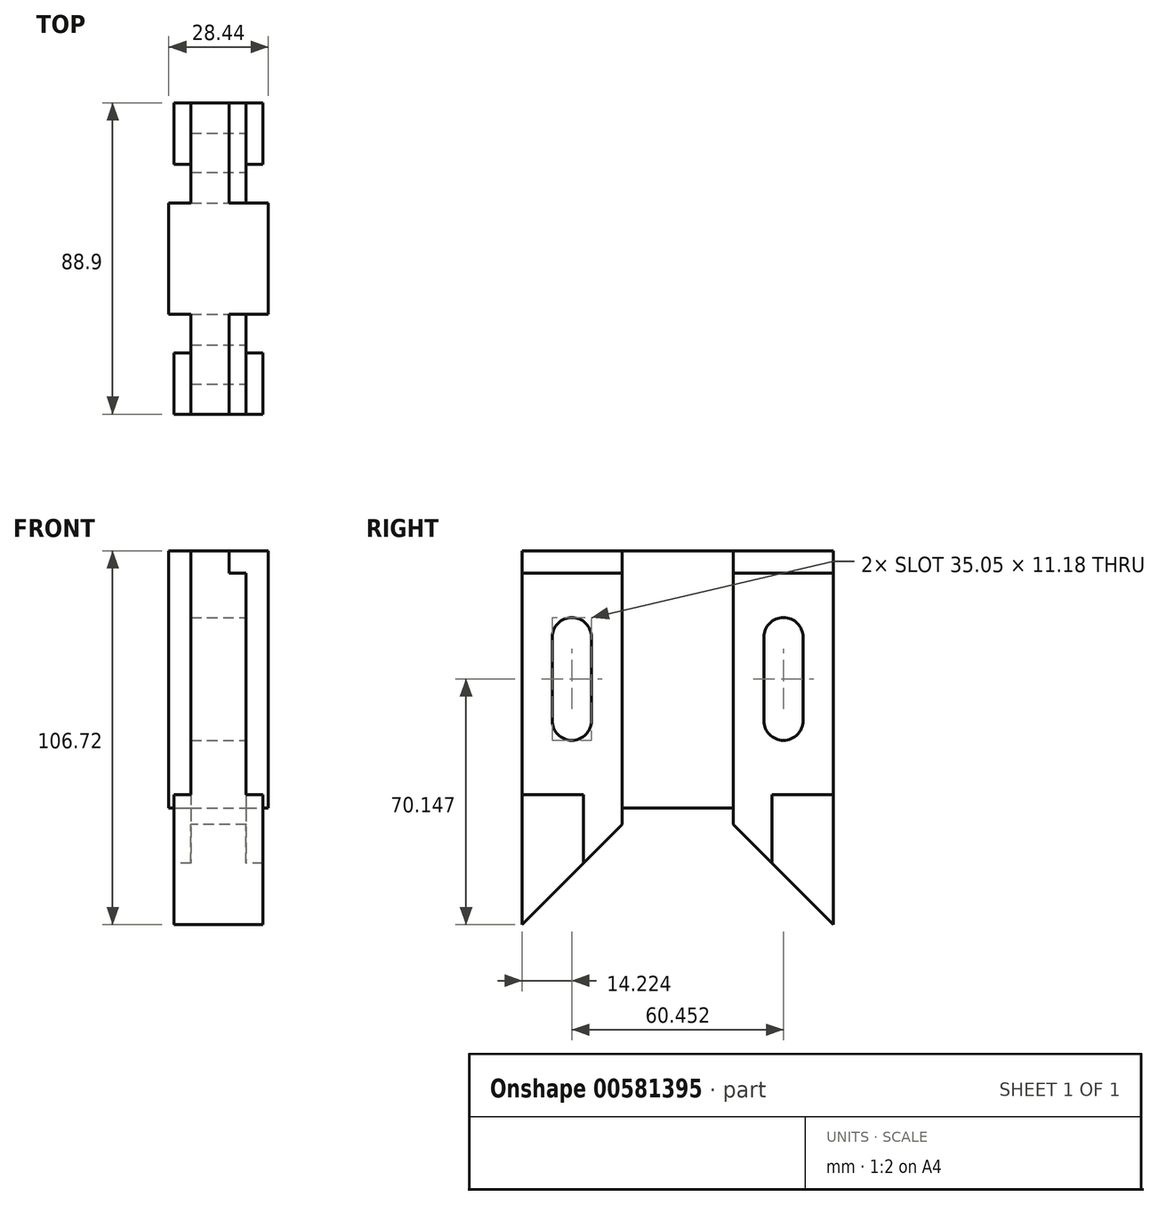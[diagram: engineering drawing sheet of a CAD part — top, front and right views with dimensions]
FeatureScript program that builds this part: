
annotation { "Feature Type Name" : "Feature", "Feature Type Description" : "" }
export const myFeature = defineFeature(function(context is Context, id is Id, definition is map)
    precondition{}
    {
        {
            var Q0;
            Q0=qCreatedBy(makeId("Front.planeOp"),FACE);
            var sketch = newSketch(context, id + "F0", { "sketchPlane" : qUnion([Q0])});
            skLineSegment(sketch, "E0.bottom", {"start": v(-14.22, -36.7) * mm, "end": v(14.22, -36.7) * mm});
            skLineSegment(sketch, "E0.top", {"start": v(-14.22, 36.7) * mm, "end": v(14.22, 36.7) * mm});
            skLineSegment(sketch, "E0.left", {"start": v(-14.22, -36.7) * mm, "end": v(-14.22, 36.7) * mm});
            skLineSegment(sketch, "E0.right", {"start": v(14.22, -36.7) * mm, "end": v(14.22, 36.7) * mm});
            skPoint(sketch, "E0.middle", {"position": v(0, 0) * mm});
            skLineSegment(sketch, "E1", {"start": v(0, 38.88) * mm, "end": v(0, -46.1) * mm, "construction": true});
            skPoint(sketch, "E1.endSnap0", {"position": v(0, -36.7) * mm});
            skSolve(sketch);
        }
        {
            var Q0;
            Q0 = qSketchRegion(id + "F0", true);
            extrude(context, id + "F1", {"entities" : qUnion([Q0]), "endBound" : BoundingType.SYMMETRIC, "depth" : 31.75 * mm, "offsetDistance" : 25.4 * mm});
        }
        {
            var Q0;
            Q0=qCreatedBy(makeId("Right.planeOp"),FACE);
            var sketch = newSketch(context, id + "F2", { "sketchPlane" : qUnion([Q0])});
            skLineSegment(sketch, "E2", {"start": v(-15.88, 36.7) * mm, "end": v(-44.45, 36.7) * mm});
            skLineSegment(sketch, "E3", {"start": v(-44.45, 36.7) * mm, "end": v(-44.45, 30.35) * mm});
            skLineSegment(sketch, "E4", {"start": v(-44.45, 30.35) * mm, "end": v(-15.88, 30.35) * mm});
            skLineSegment(sketch, "E5", {"start": v(-15.88, 30.35) * mm, "end": v(-15.88, 36.7) * mm});
            skLineSegment(sketch, "E6", {"start": v(-44.45, 30.35) * mm, "end": v(-44.45, -32.9) * mm});
            skLineSegment(sketch, "E7", {"start": v(-44.45, -32.9) * mm, "end": v(-26.92, -32.9) * mm});
            skLineSegment(sketch, "E8", {"start": v(-26.92, -32.9) * mm, "end": v(-26.92, -52.49) * mm});
            skLineSegment(sketch, "E9", {"start": v(-15.88, 36.7) * mm, "end": v(-15.88, -41.44) * mm});
            skLineSegment(sketch, "E10", {"start": v(-26.92, -52.49) * mm, "end": v(-15.87, -41.44) * mm});
            skPoint(sketch, "E11.0.1.end.orphan", {"position": v(-15.88, -36.7) * mm});
            skPoint(sketch, "E11.0.0.end.orphan", {"position": v(15.88, -36.7) * mm});
            skPoint(sketch, "E11.0.3.end.orphan", {"position": v(15.88, 36.7) * mm});
            skLineSegment(sketch, "E12.0.2", {"start": v(-15.88, -36.7) * mm, "end": v(-15.88, 36.7) * mm});
            skLineSegment(sketch, "E13", {"start": v(-78.92, 0) * mm, "end": v(0, 0) * mm, "construction": true});
            skLineSegment(sketch, "E14", {"start": v(0, 49.12) * mm, "end": v(0, -58.82) * mm, "construction": true});
            skLineSegment(sketch, "E15.left", {"start": v(-15.88, 36.7) * mm, "end": v(-15.87, -41.44) * mm});
            skLineSegment(sketch, "E15.right", {"start": v(-44.45, 36.7) * mm, "end": v(-44.45, -32.9) * mm});
            skPoint(sketch, "E16.end.orphan", {"position": v(-17.95, -70.02) * mm});
            skPoint(sketch, "E17.orphan", {"position": v(-44.45, -70.02) * mm});
            skSolve(sketch);
        }
        {
            var Q0;
            {var subQ5=sQuery(id+"F2.wireOp",EDGE,"E4");Q0=makeQuery(id+"F2.imprint","IMPRINT",FACE,{"disambiguationData":[TD([[makeQuery(id+"F2.imprint","IMPRINT",EDGE,{"derivedFrom":subQ5}),-1.0]])]});}
            var Q1;
            {var subQ0=sQuery(id+"F2.wireOp",EDGE,"E4");Q1=makeQuery(id+"F2.imprint","IMPRINT",FACE,{"disambiguationData":[TD([[makeQuery(id+"F2.imprint","IMPRINT",EDGE,{"derivedFrom":subQ0}),1.0]])]});}
            extrude(context, id + "F3", {"entities" : qUnion([Q0, Q1]), "operationType" : NewBodyOperationType.ADD, "endBound" : BoundingType.SYMMETRIC, "depth" : 15.75 * mm, "offsetDistance" : 25.4 * mm});
        }
        {
            var Q0;
            Q0=makeQuery(id+"F3.opExtrude","CAP_FACE",FACE,{"disambiguationData":[OSD([sQuery(id+"F2.wireOp",EDGE,"E7"),sQuery(id+"F2.wireOp",EDGE,"E8"),sQuery(id+"F2.wireOp",EDGE,"E10"),sQuery(id+"F2.wireOp",EDGE,"E2"),sQuery(id+"F2.wireOp",EDGE,"E15.left"),sQuery(id+"F2.wireOp",EDGE,"E15.right")])],"isStart":false});
            cPlane(context, id + "F4", {"entities" : qUnion([Q0]), "cplaneType" : CPlaneType.OFFSET, "offset" : 0 * mm, "width" : 152.4 * mm, "height" : 152.4 * mm});
        }
        {
            var Q0;
            Q0=qCreatedBy(id+"F4.planeOp",FACE);
            var sketch = newSketch(context, id + "F5", { "sketchPlane" : qUnion([Q0])});
            skLineSegment(sketch, "E18.0.0", {"start": v(-15.88, 30.35) * mm, "end": v(-15.88, 36.7) * mm});
            skLineSegment(sketch, "E18.0.1", {"start": v(-15.88, 36.7) * mm, "end": v(-44.45, 36.7) * mm});
            skLineSegment(sketch, "E18.0.2", {"start": v(-44.45, 36.7) * mm, "end": v(-44.45, 30.35) * mm});
            skLineSegment(sketch, "E19", {"start": v(-44.45, 30.35) * mm, "end": v(-15.88, 30.35) * mm});
            skPoint(sketch, "E18.0.3.start.orphan", {"position": v(-44.45, -32.9) * mm});
            skPoint(sketch, "E18.0.4.start.orphan", {"position": v(-26.92, -32.9) * mm});
            skPoint(sketch, "E18.0.5.start.orphan", {"position": v(-26.92, -52.49) * mm});
            skPoint(sketch, "E18.0.6.end.orphan", {"position": v(-15.87, -36.7) * mm});
            skPoint(sketch, "E18.0.6.start.orphan", {"position": v(-15.87, -41.44) * mm});
            skSolve(sketch);
        }
        {
            var Q0;
            Q0=makeQuery(id+"F5.imprint","IMPRINT",FACE,{"disambiguationData":[TD([[makeQuery(id+"F5.imprint","IMPRINT",EDGE,{"derivedFrom":sQuery(id+"F5.wireOp",EDGE,"E18.0.1")}),1.0]])]});
            extrude(context, id + "F6", {"entities" : qUnion([Q0]), "operationType" : NewBodyOperationType.REMOVE, "oppositeDirection" : true, "depth" : 4.83 * mm, "offsetDistance" : 25.4 * mm});
        }
        {
            var Q0;
            Q0=qCreatedBy(makeId("Right.planeOp"),FACE);
            var sketch = newSketch(context, id + "F7", { "sketchPlane" : qUnion([Q0])});
            skLineSegment(sketch, "E20.0.2", {"start": v(-44.45, -32.9) * mm, "end": v(-26.92, -32.9) * mm});
            skLineSegment(sketch, "E20.0.3", {"start": v(-26.92, -32.9) * mm, "end": v(-26.92, -52.49) * mm});
            skLineSegment(sketch, "E20.0.4", {"start": v(-26.92, -52.49) * mm, "end": v(-15.87, -41.44) * mm});
            skLineSegment(sketch, "E21", {"start": v(-44.45, -32.9) * mm, "end": v(-44.45, -70.02) * mm});
            skLineSegment(sketch, "E22", {"start": v(-44.45, -70.02) * mm, "end": v(-26.92, -52.49) * mm});
            skPoint(sketch, "E20.0.0.start.orphan", {"position": v(-15.88, 30.35) * mm});
            skPoint(sketch, "E20.0.1.start.orphan", {"position": v(-44.45, 30.35) * mm});
            skPoint(sketch, "E20.0.5.end.orphan", {"position": v(-15.87, -36.7) * mm});
            skLineSegment(sketch, "E23", {"start": v(0, 0) * mm, "end": v(0, -72.41) * mm, "construction": true});
            skSolve(sketch);
        }
        {
            var Q0;
            Q0 = qSketchRegion(id + "F7", true);
            extrude(context, id + "F8", {"entities" : qUnion([Q0]), "operationType" : NewBodyOperationType.ADD, "endBound" : BoundingType.SYMMETRIC, "depth" : 25.4 * mm, "offsetDistance" : 25.4 * mm});
        }
        {
            var Q0;
            Q0=qCreatedBy(makeId("Right.planeOp"),FACE);
            var sketch = newSketch(context, id + "F9", { "sketchPlane" : qUnion([Q0])});
            skLineSegment(sketch, "E24", {"start": v(0, 60) * mm, "end": v(0, -71.52) * mm, "construction": true});
            skSolve(sketch);
        }
        {
            var Q0;
            Q0=makeQuery(id+"F1.opExtrude","SWEPT_BODY",BODY,{"disambiguationData":[OSD([sQuery(id+"F0.wireOp",EDGE,"E0.bottom"),sQuery(id+"F0.wireOp",EDGE,"E0.top"),sQuery(id+"F0.wireOp",EDGE,"E0.left"),sQuery(id+"F0.wireOp",EDGE,"E0.right")])]});
            var Q1;
            Q1=qCreatedBy(makeId("Front.planeOp"),FACE);
            mirror(context, id + "F10", {"operationType" : NewBodyOperationType.ADD, "entities" : qUnion([Q0]), "mirrorPlane" : qUnion([Q1])});
        }
        {
            var Q0;
            Q0=qCreatedBy(id+"F4.planeOp",FACE);
            var sketch = newSketch(context, id + "F11", { "sketchPlane" : qUnion([Q0])});
            skLineSegment(sketch, "E25.bottom", {"start": v(-30.23, 17.65) * mm, "end": v(-30.23, 17.65) * mm});
            skLineSegment(sketch, "E25.top", {"start": v(-30.23, -17.4) * mm, "end": v(-30.23, -17.4) * mm});
            skLineSegment(sketch, "E25.left", {"start": v(-35.81, 12.07) * mm, "end": v(-35.81, -11.81) * mm});
            skLineSegment(sketch, "E25.right", {"start": v(-24.64, 12.07) * mm, "end": v(-24.64, -11.81) * mm});
            skPoint(sketch, "E26.visualSharp", {"position": v(-35.81, 17.65) * mm});
            skArc(sketch, "E26.filletArc", {"start": v(-30.23, 17.65) * mm, "mid": v(-34.18, 16.02) * mm, "end": v(-35.81, 12.07) * mm});
            skPoint(sketch, "E27.visualSharp", {"position": v(-24.64, 17.65) * mm});
            skArc(sketch, "E27.filletArc", {"start": v(-24.64, 12.07) * mm, "mid": v(-26.27, 16.02) * mm, "end": v(-30.23, 17.65) * mm});
            skPoint(sketch, "E28.visualSharp", {"position": v(-35.81, -17.4) * mm});
            skArc(sketch, "E28.filletArc", {"start": v(-35.81, -11.81) * mm, "mid": v(-34.18, -15.76) * mm, "end": v(-30.23, -17.4) * mm});
            skPoint(sketch, "E29.visualSharp", {"position": v(-24.64, -17.4) * mm});
            skArc(sketch, "E29.filletArc", {"start": v(-30.23, -17.4) * mm, "mid": v(-26.27, -15.76) * mm, "end": v(-24.64, -11.81) * mm});
            skLineSegment(sketch, "E30.0", {"start": v(0, 60) * mm, "end": v(0, -71.52) * mm, "construction": true});
            skArc(sketch, "E31.MirrorCS", {"start": v(35.81, -11.81) * mm, "mid": v(34.18, -15.76) * mm, "end": v(30.23, -17.4) * mm});
            skArc(sketch, "E32.MirrorCS", {"start": v(30.23, 17.65) * mm, "mid": v(34.18, 16.02) * mm, "end": v(35.81, 12.07) * mm});
            skArc(sketch, "E33.MirrorCS", {"start": v(24.64, 12.07) * mm, "mid": v(26.27, 16.02) * mm, "end": v(30.23, 17.65) * mm});
            skArc(sketch, "E34.MirrorCS", {"start": v(30.23, -17.4) * mm, "mid": v(26.27, -15.76) * mm, "end": v(24.64, -11.81) * mm});
            skPoint(sketch, "E35.MirrorP", {"position": v(24.64, 17.65) * mm});
            skPoint(sketch, "E36.MirrorP", {"position": v(24.64, -17.4) * mm});
            skLineSegment(sketch, "E37.MirrorCS", {"start": v(30.23, -17.4) * mm, "end": v(30.23, -17.4) * mm});
            skPoint(sketch, "E38.MirrorP", {"position": v(35.81, 17.65) * mm});
            skPoint(sketch, "E39.MirrorP", {"position": v(35.81, -17.4) * mm});
            skLineSegment(sketch, "E40.MirrorCS", {"start": v(35.81, 12.07) * mm, "end": v(35.81, -11.81) * mm});
            skLineSegment(sketch, "E41.MirrorCS", {"start": v(24.64, 12.07) * mm, "end": v(24.64, -11.81) * mm});
            skLineSegment(sketch, "E42.MirrorCS", {"start": v(30.23, 17.65) * mm, "end": v(30.23, 17.65) * mm});
            skLineSegment(sketch, "E43", {"start": v(-44.45, 40.34) * mm, "end": v(-44.45, -83.08) * mm, "construction": true});
            skSolve(sketch);
        }
        {
            var Q0;
            Q0 = qSketchRegion(id + "F11", true);
            extrude(context, id + "F12", {"entities" : qUnion([Q0]), "operationType" : NewBodyOperationType.REMOVE, "oppositeDirection" : true, "depth" : 40.13 * mm, "offsetDistance" : 25.4 * mm});
        }
    });
